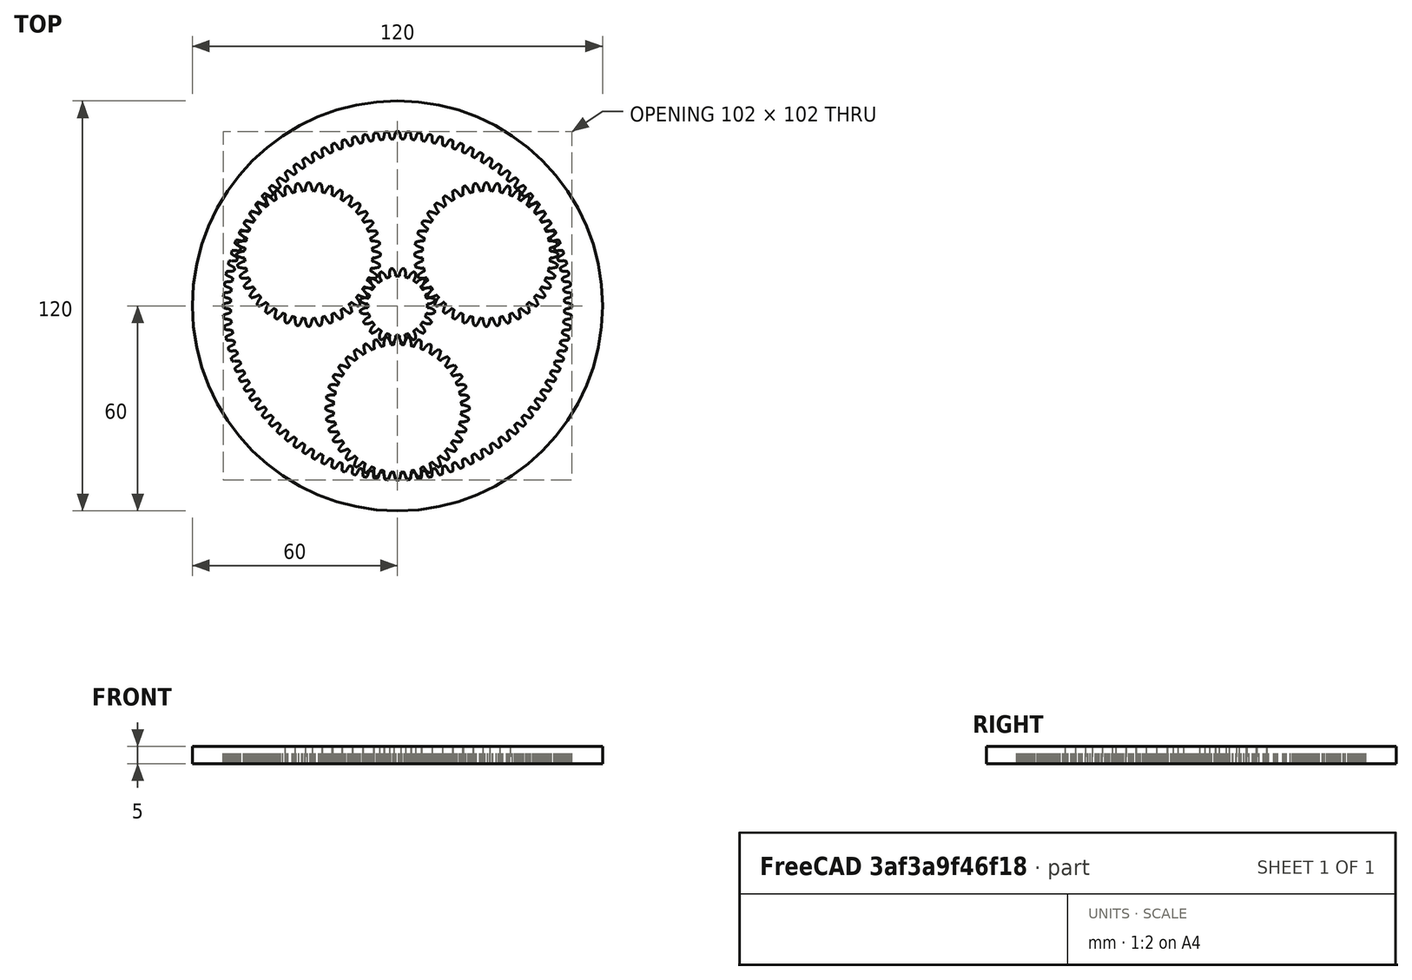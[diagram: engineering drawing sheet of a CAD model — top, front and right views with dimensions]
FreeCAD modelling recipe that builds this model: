
FCSTD DOCUMENT  (FreeCAD 0.18R14555 (Git shallow))
Label: FREECAD #43 - PLANETARIA
License: All rights reserved
LicenseURL: http://en.wikipedia.org/wiki/All_rights_reserved
objects: Part::FeaturePython×5, Part::Cylinder×1, Part::Cut×1
note: 7 computed .brp shape members not serialized (recipe doc carries the construction recipe); baked Part::Feature solids carry a one-line shape summary decoded from their .brp

FEATURE [Part::FeaturePython] InvoluteGear  # WARN: FeaturePython — macro-defined, semantics opaque (R4)
  Placement = pos=(0,0,0) rot=(0,0,1;0.15708rad)
  backlash = 0
  beta = 0
  clearance = 0.25
  double_helix = false
  head = 0
  height = 5
  module = 1
  numpoints = 6
  pressure_angle = 20
  reversed_backlash = false
  shift = 0
  simple = false
  teeth = 20
  undercut = false
FEATURE [Part::FeaturePython] InvoluteGear001  # WARN: FeaturePython — macro-defined, semantics opaque (R4)
  Placement = pos=(0,-30,0) rot=(0,0,1;0rad)
  backlash = 0
  beta = 0
  clearance = 0.25
  double_helix = false
  head = 0
  height = 5
  module = 1
  numpoints = 6
  pressure_angle = 20
  reversed_backlash = false
  shift = 0
  simple = false
  teeth = 40
  undercut = false
FEATURE [Part::FeaturePython] InvoluteGear002  # WARN: FeaturePython — macro-defined, semantics opaque (R4)
  Placement = pos=(-26,15,0) rot=(0,0,1;0rad)
  backlash = 0
  beta = 0
  clearance = 0.25
  double_helix = false
  head = 0
  height = 5
  module = 1
  numpoints = 6
  pressure_angle = 20
  reversed_backlash = false
  shift = 0
  simple = false
  teeth = 40
  undercut = false
FEATURE [Part::FeaturePython] CycloideGear  # WARN: FeaturePython — macro-defined, semantics opaque (R4)
  backlash = 0
  beta = 0
  clearance = 0.25
  double_helix = false
  height = 5
  inner_diameter = 5
  module = 1
  numpoints = 15
  outer_diameter = 5
  teeth = 100
FEATURE [Part::FeaturePython] InvoluteGear003  # WARN: FeaturePython — macro-defined, semantics opaque (R4)
  Placement = pos=(26,15,0) rot=(0,0,1;0rad)
  backlash = 0
  beta = 0
  clearance = 0.25
  double_helix = false
  head = 0
  height = 5
  module = 1
  numpoints = 6
  pressure_angle = 20
  reversed_backlash = false
  shift = 0
  simple = false
  teeth = 40
  undercut = false
FEATURE [Part::Cylinder] Cylinder  label="Cilindro"
  Angle = 360
  AttacherType = Attacher::AttachEngine3D
  Height = 5
  Radius = 60
FEATURE [Part::Cut] Cut
  Base = -> Cylinder
  Tool = -> CycloideGear
